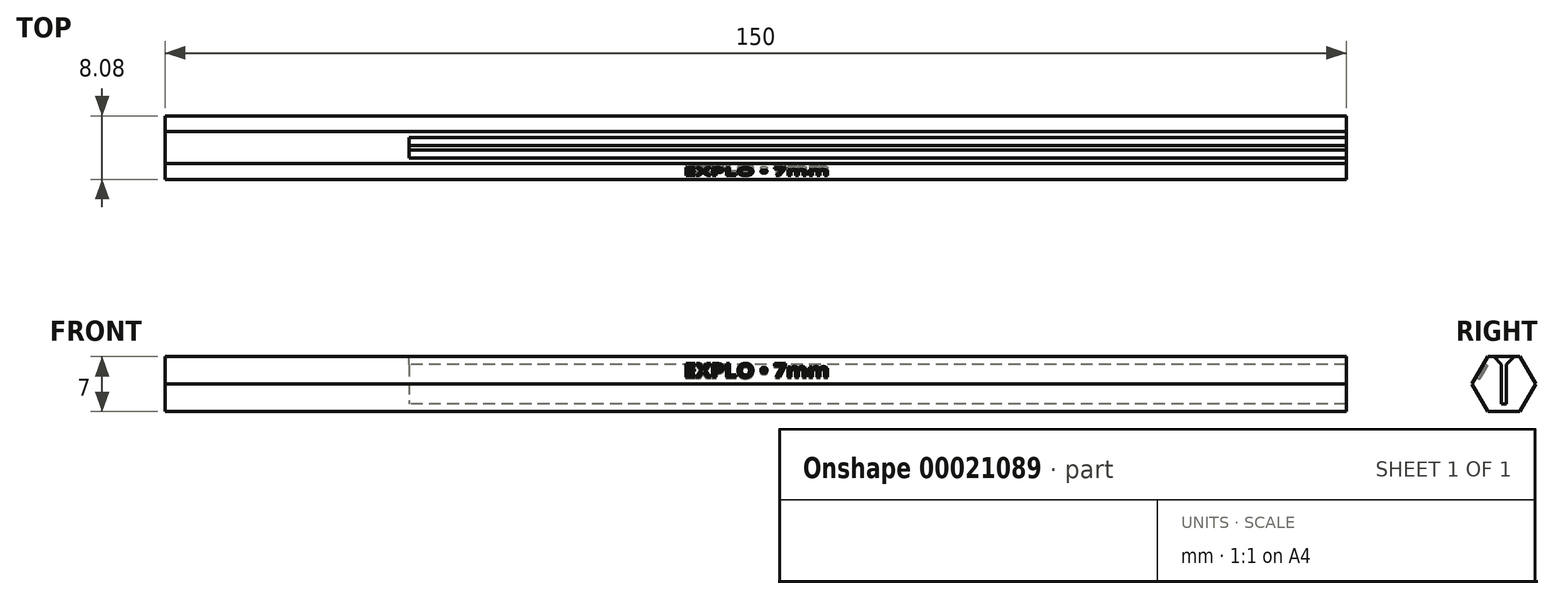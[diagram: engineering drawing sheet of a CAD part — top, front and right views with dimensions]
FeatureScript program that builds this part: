
annotation { "Feature Type Name" : "Feature", "Feature Type Description" : "" }
export const myFeature = defineFeature(function(context is Context, id is Id, definition is map)
    precondition{}
    {
        {
            assignVariable(context, id + "F0", {"name" : "SlotFloorDepth", "anyValue" : 1});
        }
        {
            var Q0;
            Q0=qCreatedBy(makeId("Right.planeOp"),FACE);
            var sketch = newSketch(context, id + "F1", { "sketchPlane" : qUnion([Q0])});
            skCircle(sketch, "E0.cCircle", {"center": v(0, 3.5) * mm, "radius": 3.5 * mm, "construction": true});
            skLineSegment(sketch, "E0.0", {"start": v(2.02, 7) * mm, "end": v(4.04, 3.5) * mm});
            skLineSegment(sketch, "E0.1", {"start": v(4.04, 3.5) * mm, "end": v(2.02, 0) * mm});
            skLineSegment(sketch, "E0.2", {"start": v(2.02, 0) * mm, "end": v(-2.02, 0) * mm});
            skLineSegment(sketch, "E0.3", {"start": v(-2.02, 0) * mm, "end": v(-4.04, 3.5) * mm});
            skLineSegment(sketch, "E0.4", {"start": v(-4.04, 3.5) * mm, "end": v(-2.02, 7) * mm});
            skLineSegment(sketch, "E0.5", {"start": v(-2.02, 7) * mm, "end": v(2.02, 7) * mm});
            skPoint(sketch, "E0.0.midPoint", {"position": v(3.03, 5.25) * mm});
            skLineSegment(sketch, "E1", {"start": v(-2.6, 1) * mm, "end": v(2.6, 1) * mm});
            skLineSegment(sketch, "E2", {"start": v(0, 0) * mm, "end": v(0, 7) * mm, "construction": true});
            skLineSegment(sketch, "E3", {"start": v(-0.3, 7) * mm, "end": v(-0.3, 0) * mm});
            skLineSegment(sketch, "E4.MirrorCS", {"start": v(0.3, 7) * mm, "end": v(0.3, 0) * mm});
            skSolve(sketch);
        }
        {
            assignVariable(context, id + "F2", {"name" : "Length", "anyValue" : 120});
        }
        {
            var Q0;
            {var subQ7=sQuery(id+"F1.wireOp",EDGE,"E0.4");Q0=makeQuery(id+"F1.imprint","IMPRINT",FACE,{"disambiguationData":[TD([[makeQuery(id+"F1.imprint","IMPRINT",EDGE,{"derivedFrom":subQ7}),-1.0]])]});}
            var Q1;
            {var subQ7=sQuery(id+"F1.wireOp",EDGE,"E0.0");Q1=makeQuery(id+"F1.imprint","IMPRINT",FACE,{"disambiguationData":[TD([[makeQuery(id+"F1.imprint","IMPRINT",EDGE,{"derivedFrom":subQ7}),-1.0]])]});}
            var Q2;
            {var subQ3=sQuery(id+"F1.wireOp",EDGE,"E0.2");var subQ5=sQuery(id+"F1.wireOp",EDGE,"E0.3");var subQ7=makeQuery(id+"F1.imprint","INTERSECT",VERTEX,{"derivedFrom":[subQ3,subQ5]});Q2=makeQuery(id+"F1.imprint","IMPRINT",FACE,{"disambiguationData":[TD([[makeQuery(id+"F1.imprint","IMPRINT",EDGE,{"disambiguationData":[TD([[subQ7,1.0]])],"derivedFrom":subQ3}),-1.0]])]});}
            var Q3;
            {var subQ3=sQuery(id+"F1.wireOp",EDGE,"E0.2");var subQ5=sQuery(id+"F1.wireOp",EDGE,"E3");var subQ7=makeQuery(id+"F1.imprint","INTERSECT",VERTEX,{"derivedFrom":[subQ3,subQ5]});Q3=makeQuery(id+"F1.imprint","IMPRINT",FACE,{"disambiguationData":[TD([[makeQuery(id+"F1.imprint","IMPRINT",EDGE,{"disambiguationData":[TD([[subQ7,1.0]])],"derivedFrom":subQ3}),-1.0]])]});}
            var Q4;
            {var subQ3=sQuery(id+"F1.wireOp",EDGE,"E0.2");var subQ5=sQuery(id+"F1.wireOp",EDGE,"E0.1");var subQ7=makeQuery(id+"F1.imprint","INTERSECT",VERTEX,{"derivedFrom":[subQ5,subQ3]});Q4=makeQuery(id+"F1.imprint","IMPRINT",FACE,{"disambiguationData":[TD([[makeQuery(id+"F1.imprint","IMPRINT",EDGE,{"disambiguationData":[TD([[subQ7,1.0]])],"derivedFrom":subQ5}),-1.0]])]});}
            extrude(context, id + "F3", {"entities" : qUnion([Q0, Q1, Q2, Q3, Q4]), "depth" : (getVariable(context, 'Length')) * mm});
        }
        {
            var Q0;
            {var subQ0=sQuery(id+"F1.wireOp",EDGE,"E3");var subQ3=sQuery(id+"F1.wireOp",EDGE,"E0.5");var subQ4=makeQuery(id+"F1.imprint","INTERSECT",VERTEX,{"derivedFrom":[subQ3,subQ0]});Q0=makeQuery(id+"F1.imprint","IMPRINT",FACE,{"disambiguationData":[TD([[makeQuery(id+"F1.imprint","IMPRINT",EDGE,{"disambiguationData":[TD([[subQ4,-1.0]])],"derivedFrom":subQ3}),-1.0]])]});}
            var Q1;
            {var subQ3=sQuery(id+"F1.wireOp",EDGE,"E0.2");var subQ5=sQuery(id+"F1.wireOp",EDGE,"E0.1");var subQ7=makeQuery(id+"F1.imprint","INTERSECT",VERTEX,{"derivedFrom":[subQ5,subQ3]});Q1=makeQuery(id+"F1.imprint","IMPRINT",FACE,{"disambiguationData":[TD([[makeQuery(id+"F1.imprint","IMPRINT",EDGE,{"disambiguationData":[TD([[subQ7,1.0]])],"derivedFrom":subQ5}),-1.0]])]});}
            var Q2;
            {var subQ3=sQuery(id+"F1.wireOp",EDGE,"E0.2");var subQ5=sQuery(id+"F1.wireOp",EDGE,"E0.3");var subQ7=makeQuery(id+"F1.imprint","INTERSECT",VERTEX,{"derivedFrom":[subQ3,subQ5]});Q2=makeQuery(id+"F1.imprint","IMPRINT",FACE,{"disambiguationData":[TD([[makeQuery(id+"F1.imprint","IMPRINT",EDGE,{"disambiguationData":[TD([[subQ7,1.0]])],"derivedFrom":subQ3}),-1.0]])]});}
            var Q3;
            {var subQ7=sQuery(id+"F1.wireOp",EDGE,"E0.0");Q3=makeQuery(id+"F1.imprint","IMPRINT",FACE,{"disambiguationData":[TD([[makeQuery(id+"F1.imprint","IMPRINT",EDGE,{"derivedFrom":subQ7}),-1.0]])]});}
            var Q4;
            {var subQ7=sQuery(id+"F1.wireOp",EDGE,"E0.4");Q4=makeQuery(id+"F1.imprint","IMPRINT",FACE,{"disambiguationData":[TD([[makeQuery(id+"F1.imprint","IMPRINT",EDGE,{"derivedFrom":subQ7}),-1.0]])]});}
            var Q5;
            {var subQ3=sQuery(id+"F1.wireOp",EDGE,"E0.2");var subQ5=sQuery(id+"F1.wireOp",EDGE,"E3");var subQ7=makeQuery(id+"F1.imprint","INTERSECT",VERTEX,{"derivedFrom":[subQ3,subQ5]});Q5=makeQuery(id+"F1.imprint","IMPRINT",FACE,{"disambiguationData":[TD([[makeQuery(id+"F1.imprint","IMPRINT",EDGE,{"disambiguationData":[TD([[subQ7,1.0]])],"derivedFrom":subQ3}),-1.0]])]});}
            extrude(context, id + "F4", {"entities" : qUnion([Q0, Q1, Q2, Q3, Q4, Q5]), "operationType" : NewBodyOperationType.ADD, "oppositeDirection" : true, "depth" : 30 * mm, "hasSecondDirection" : true, "secondDirectionOppositeDirection" : false, "secondDirectionDepth" : 1 * mm});
        }
        {
            var Q0;
            Q0=makeQuery(id+"F3.opExtrude","SWEPT_EDGE",EDGE,{"disambiguationData":[OSD([sQuery(id+"F1.wireOp",EDGE,"E0.5"),sQuery(id+"F1.wireOp",EDGE,"E3")])]});
            var Q1;
            Q1=makeQuery(id+"F3.opExtrude","SWEPT_EDGE",EDGE,{"disambiguationData":[OSD([sQuery(id+"F1.wireOp",EDGE,"E0.5"),sQuery(id+"F1.wireOp",EDGE,"E4.MirrorCS")])]});
            chamfer(context, id + "F5", {"entities" : qUnion([Q0, Q1]), "width" : (getVariable(context, 'SlotFloorDepth')) * mm, "tangentPropagation" : true});
        }
        {
            var Q0;
            {var subQ0=sQuery(id+"F1.wireOp",EDGE,"E0.4");Q0=makeQuery(id+"F4.boolean.opBoolean","MERGE",FACE,{"derivedFrom":[makeQuery(id+"F3.opExtrude","SWEPT_FACE",FACE,{"disambiguationData":[OSD([subQ0])]}),makeQuery(id+"F4.opExtrude","SWEPT_FACE",FACE,{"disambiguationData":[OSD([subQ0])]})]});}
            var sketch = newSketch(context, id + "F6", { "sketchPlane" : qUnion([Q0])});
            skLineSegment(sketch, "E5.0", {"start": v(-30, 1.01) * mm, "end": v(-30, 5.05) * mm, "construction": true});
            skLineSegment(sketch, "E5.1", {"start": v(120, 1.01) * mm, "end": v(-30, 1.01) * mm, "construction": true});
            skLineSegment(sketch, "E5.2", {"start": v(120, 5.05) * mm, "end": v(-30, 5.05) * mm, "construction": true});
            skLineSegment(sketch, "E5.3", {"start": v(120, 1.01) * mm, "end": v(120, 5.05) * mm, "construction": true});
            skText(sketch, "E6", { "text": "EXPLO • 7mm", "fontName": "OpenSans-Bold.ttf"});
            skLineSegment(sketch, "E7", {"start": v(120, 3.03) * mm, "end": v(-30, 3.03) * mm, "construction": true});
            skLineSegment(sketch, "E8", {"start": v(45, 5.05) * mm, "end": v(45, 1.01) * mm, "construction": true});
            skPoint(sketch, "E9", {"position": v(35.87, 3.03) * mm});
            const initialGuessF6  = {"E6": [0.03587, 0.00203, 1, 0, 0.002]};
            skSetInitialGuess(sketch, initialGuessF6);
            skSolve(sketch);
        }
        {
            var Q0;
            Q0 = qSketchRegion(id + "F6", true);
            extrude(context, id + "F7", {"entities" : qUnion([Q0]), "operationType" : NewBodyOperationType.REMOVE, "oppositeDirection" : true, "depth" : .5 * mm});
        }
    });
